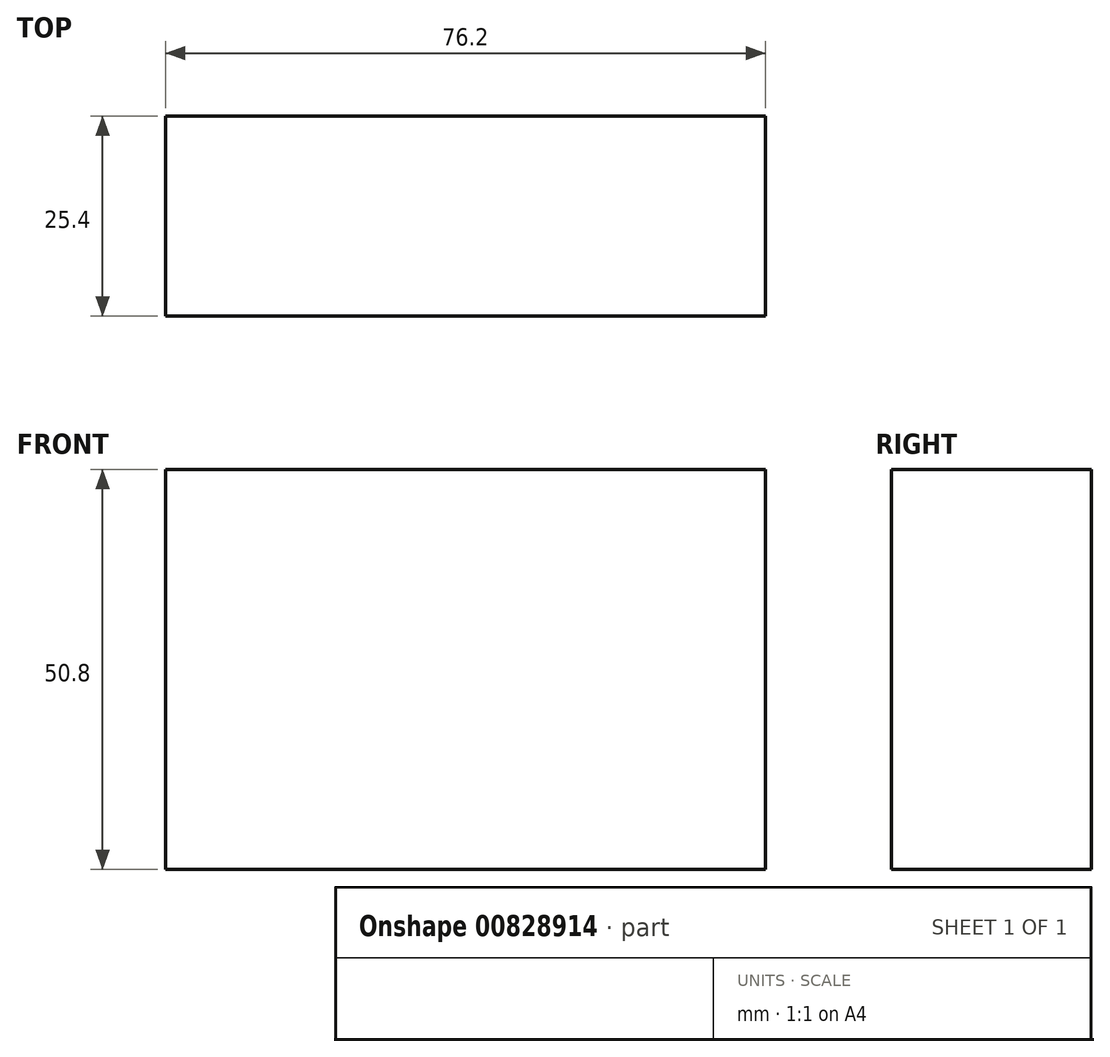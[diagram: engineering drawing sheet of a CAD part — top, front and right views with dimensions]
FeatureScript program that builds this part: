
annotation { "Feature Type Name" : "Feature", "Feature Type Description" : "" }
export const myFeature = defineFeature(function(context is Context, id is Id, definition is map)
    precondition{}
    {
        {
            var Q0;
            Q0=qCreatedBy(makeId("Front.planeOp"),FACE);
            var sketch = newSketch(context, id + "F0", { "sketchPlane" : qUnion([Q0])});
            skLineSegment(sketch, "E0.bottom", {"start": v(38.1, -25.4) * mm, "end": v(-38.1, -25.4) * mm});
            skLineSegment(sketch, "E0.top", {"start": v(38.1, 25.4) * mm, "end": v(-38.1, 25.4) * mm});
            skLineSegment(sketch, "E0.left", {"start": v(38.1, -25.4) * mm, "end": v(38.1, 25.4) * mm});
            skLineSegment(sketch, "E0.right", {"start": v(-38.1, -25.4) * mm, "end": v(-38.1, 25.4) * mm});
            skPoint(sketch, "E0.middle", {"position": v(0, 0) * mm});
            skSolve(sketch);
        }
        {
            var Q0;
            Q0 = qSketchRegion(id + "F0", true);
            extrude(context, id + "F1", {"entities" : qUnion([Q0]), "depth" : 25.4 * mm, "offsetDistance" : 25.4 * mm});
        }
    });
